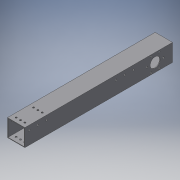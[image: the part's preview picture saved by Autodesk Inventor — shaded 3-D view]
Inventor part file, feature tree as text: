
AUTODESK INVENTOR PART (.ipt)
format: ipt  version: 2018.3 (Build 223284000, 284)  size: 205,312 bytes
history: native  units: in
note: dims shown in document units (in); Inventor stores cm internally (conversion verified against a paired STEP export)
features: extrude x5, sketch x5
ambient origin geometry x8: Origin, YZ Plane, XZ Plane, XY Plane, X Axis, Y Axis, Z Axis, Center Point
bodies: Solid1 (feature_tree)
feature tree (10):
  extrude  "Extrusion1"  Depth=2.0in
  extrude  "Extrusion2"  Depth=0.065in
  extrude  "Extrusion4"  Depth=0.065in
  extrude  "Extrusion5"  Depth=17.0in
  extrude  "Extrusion7"  Depth=2.0in
  sketch  "Sketch1"  dims[d0=2.0in d1=2.0in]
  sketch  "Sketch2"  dims[d2=0.065in d3=0.065in]
  sketch  "Sketch5"  dims[d4=0.065in d5=0.065in]
  sketch  "Sketch6"  dims[d6=17.0in d7=0.0in d8=4.5in]
  sketch  "Sketch7"  dims[d9=1.0in d10=1.0in d11=1.0in d12=1.0in d13=0.5in d14=0.2031in d15=0.2031in d16=0.2031in d19=0.2031in d20=0.2031in d21=0.2031in d22=0.5in d23=0.5in d24=0.5in d25=0.5in d26=0.5in d27=0.5in d28=11.0in d29=0.0in d36=2.0in d37=0.9375in d38=0.75in d39=0.2031in d40=1.0in d41=1.0in d42=2.3622in d44=360.0deg d46=2.0in d47=0.0in d48=1.0in d49=0.9375in d50=1.15in d51=2.0in d52=0.0in d53=0.2031in d54=1.0in d56=0.5in d57=0.2031in d58=0.2031in d59=0.5in d60=1.0in d61=0.5in d62=0.5in d65=2.0in d66=90.0deg d67=2.0in d68=2.0in d69=0.2031in d70=0.2031in d71=0.2031in d72=5.0in d73=0.0in]
